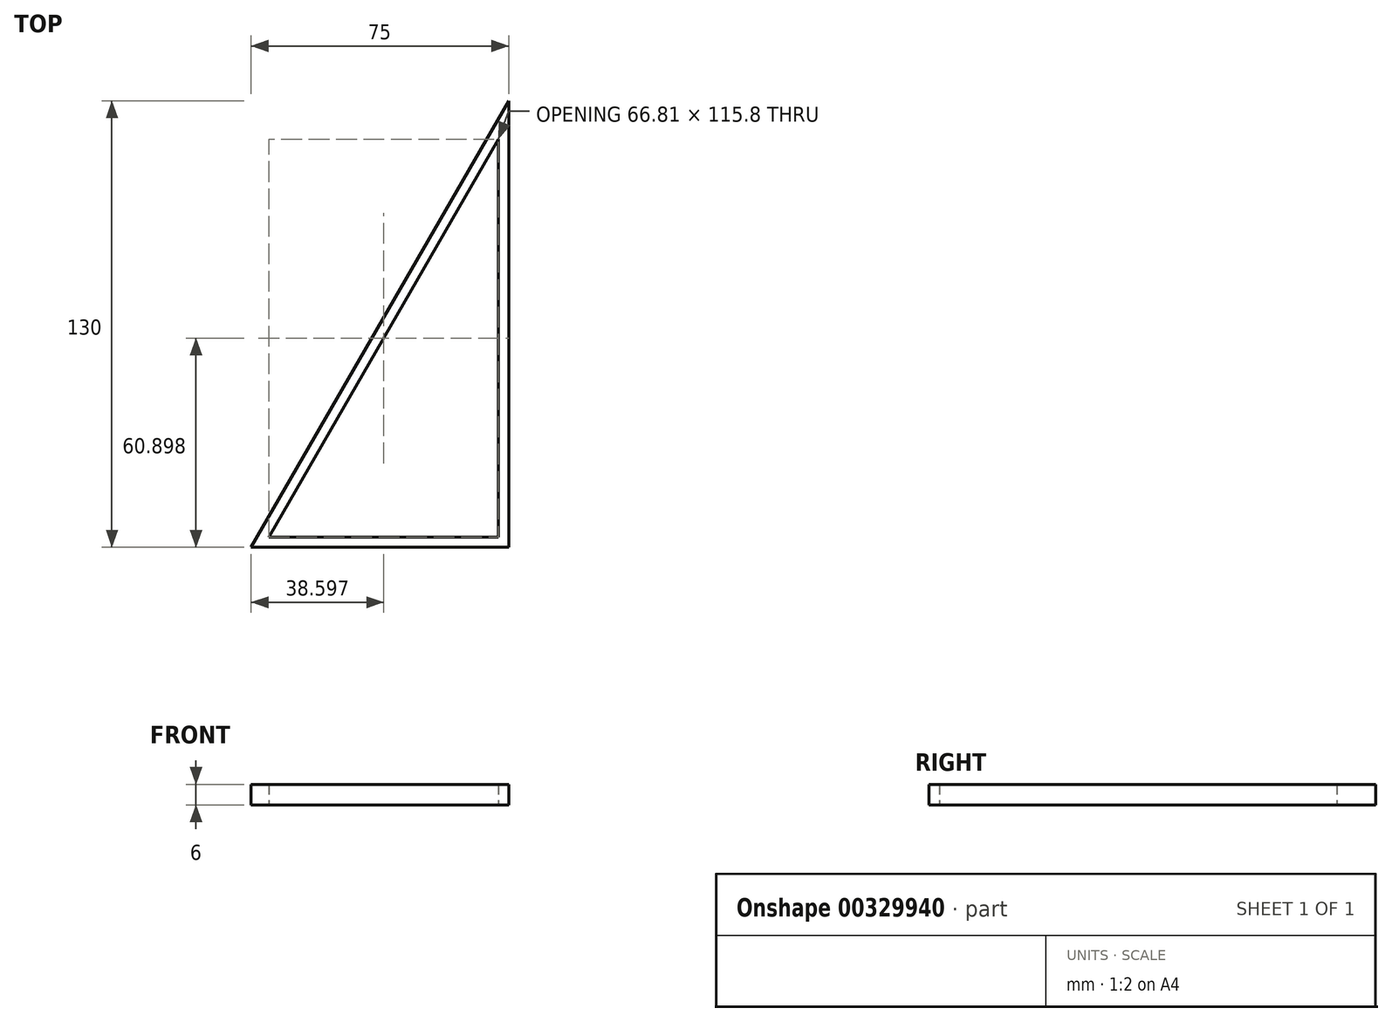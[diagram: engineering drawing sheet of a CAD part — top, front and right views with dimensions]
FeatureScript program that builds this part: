
annotation { "Feature Type Name" : "Feature", "Feature Type Description" : "" }
export const myFeature = defineFeature(function(context is Context, id is Id, definition is map)
    precondition{}
    {
        {
            var Q0;
            Q0=qCreatedBy(makeId("Top.planeOp"),FACE);
            var sketch = newSketch(context, id + "F0", { "sketchPlane" : qUnion([Q0])});
            skLineSegment(sketch, "E0", {"start": v(-18.38, 0) * mm, "end": v(56.62, 0) * mm});
            skLineSegment(sketch, "E1", {"start": v(56.62, 0) * mm, "end": v(56.62, 130) * mm});
            skLineSegment(sketch, "E2", {"start": v(56.62, 130) * mm, "end": v(-18.38, 0) * mm});
            skLineSegment(sketch, "E3.0", {"start": v(53.62, 3) * mm, "end": v(53.62, 118.8) * mm});
            skPoint(sketch, "E4", {"position": v(53.62, 124.8) * mm});
            skLineSegment(sketch, "E5.0", {"start": v(53.62, 118.8) * mm, "end": v(-13.19, 3) * mm});
            skPoint(sketch, "E6", {"position": v(56.62, 124) * mm});
            skLineSegment(sketch, "E7.0", {"start": v(-13.19, 3) * mm, "end": v(53.62, 3) * mm});
            skSolve(sketch);
        }
        {
            var Q0;
            Q0=makeQuery(id+"F0.imprint","IMPRINT",FACE,{"disambiguationData":[TD([[makeQuery(id+"F0.imprint","IMPRINT",EDGE,{"derivedFrom":sQuery(id+"F0.wireOp",EDGE,"E0")}),1.0]])]});
            extrude(context, id + "F1", {"entities" : qUnion([Q0]), "depth" : 6 * mm});
        }
    });
